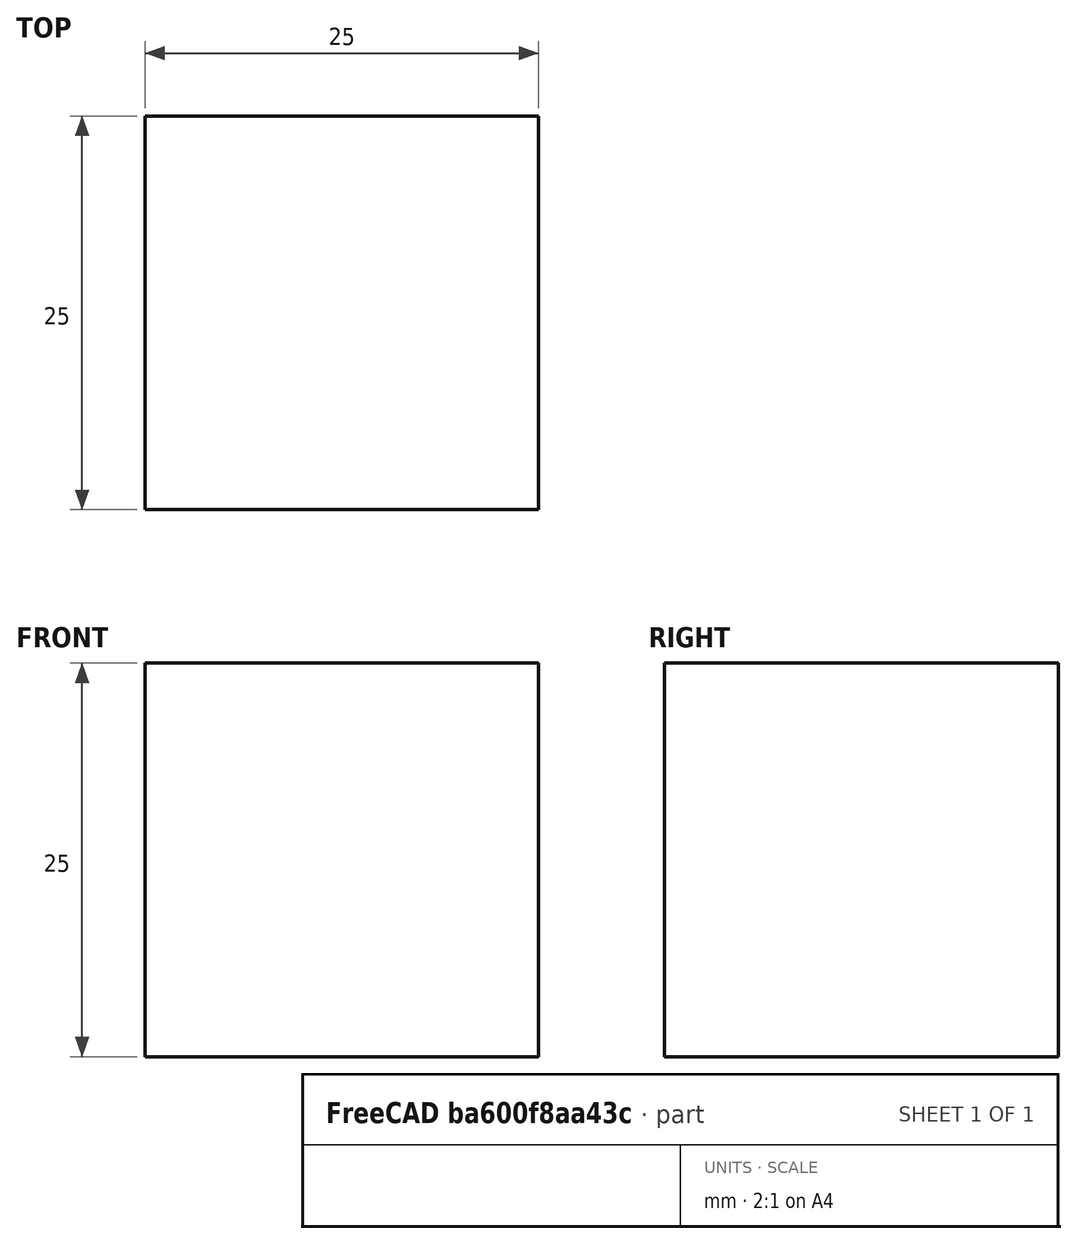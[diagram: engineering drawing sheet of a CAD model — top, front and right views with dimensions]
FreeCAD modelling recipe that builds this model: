
FCSTD DOCUMENT  (FreeCAD 0.18.4R)
Label: gripper-connector-block
License: All rights reserved
LicenseURL: http://en.wikipedia.org/wiki/All_rights_reserved
objects: Sketcher::SketchObject×1, PartDesign::Pad×1, PartDesign::Body×1
note: 4 computed .brp shape members not serialized (recipe doc carries the construction recipe); baked Part::Feature solids carry a one-line shape summary decoded from their .brp

FEATURE [Sketcher::SketchObject] Sketch
  MapMode = 5
  Support = -> [XY_Plane]
  sketch-geometry (4):
    g0: LineSegment StartX=-12.5 StartY=12.5 StartZ=0 EndX=12.5 EndY=12.5 EndZ=0
    g1: LineSegment StartX=12.5 StartY=12.5 StartZ=0 EndX=12.5 EndY=-12.5 EndZ=0
    g2: LineSegment StartX=12.5 StartY=-12.5 StartZ=0 EndX=-12.5 EndY=-12.5 EndZ=0
    g3: LineSegment StartX=-12.5 StartY=-12.5 StartZ=0 EndX=-12.5 EndY=12.5 EndZ=0
  constraints (12):
    c: Coincident(g0,g1)
    c: Coincident(g1,g2)
    c: Coincident(g2,g3)
    c: Coincident(g3,g0)
    c: Horizontal(g0)
    c: Horizontal(g2)
    c: Vertical(g1)
    c: Vertical(g3)
    c: DistanceX(g0,g0) = 25
    c: Equal(g0,g3)
    c: DistanceX(g0,g-1) = 12.5
    c: DistanceY(g2,g-1) = 12.5
FEATURE [PartDesign::Pad] Pad
  Length = 25
  Length2 = 100
  Midplane = true
  Profile = -> Sketch
  Type = 0
FEATURE [PartDesign::Body] Body
  Group = -> [Sketch,Pad]
  Origin = -> Origin
  Tip = -> Pad
